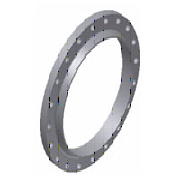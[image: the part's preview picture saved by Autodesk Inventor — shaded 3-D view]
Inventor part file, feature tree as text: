
AUTODESK INVENTOR PART (.ipt)
format: ipt  version: 2023.2 (Build 272271030, 271C)  size: 260,096 bytes
history: native  units: mm
features: sketch x2, pattern_circular x1
ambient origin geometry x8: Origin, YZ Plane, XZ Plane, XY Plane, X Axis, Y Axis, Z Axis, Center Point
bodies: Solid1 (feature_tree)
feature tree (3):
  pattern_circular  "Circular Pattern1"  Count=59  [1 undecoded]
  sketch  "Sketch1"  dims[d1=450.0mm]
  sketch  "Sketch2"  dims[d2=522.0mm d3=514.0mm d4=5.0mm d7=35.0mm d8=45.0deg d9=65.0mm d10=3.0mm d14=3.217506mm d15=464.0mm d16=7.0mm d24=90.0deg d25=23.0mm d26=275.0mm d30=10.0mm d31=0.0mm d32=240.0mm d33=360.0deg]
note: 1 required parameter value undecoded (feature->parameter linkage not recoverable at this tier; creation-order binding heuristic only, values carry confidence <= 0.55)
